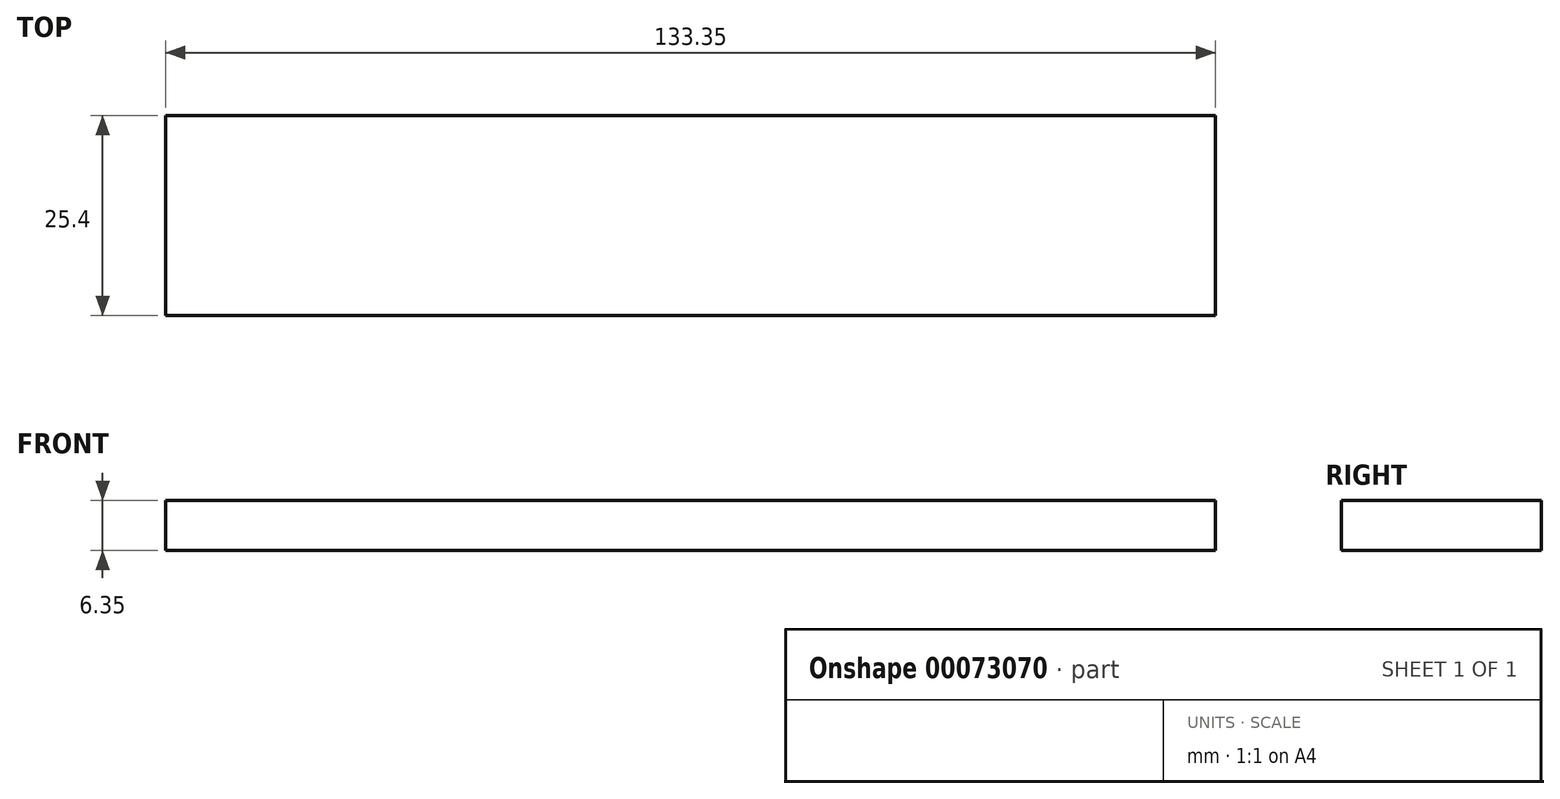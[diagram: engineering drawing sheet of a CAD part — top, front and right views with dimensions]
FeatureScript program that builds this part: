
annotation { "Feature Type Name" : "Feature", "Feature Type Description" : "" }
export const myFeature = defineFeature(function(context is Context, id is Id, definition is map)
    precondition{}
    {
        {
            var Q0;
            Q0=qCreatedBy(makeId("Top.planeOp"),FACE);
            var sketch = newSketch(context, id + "F0", { "sketchPlane" : qUnion([Q0])});
            skLineSegment(sketch, "E0.bottom", {"start": v(0, 0) * mm, "end": v(-133.35, 0) * mm});
            skLineSegment(sketch, "E0.top", {"start": v(0, 25.4) * mm, "end": v(-133.35, 25.4) * mm});
            skLineSegment(sketch, "E0.left", {"start": v(0, 0) * mm, "end": v(0, 25.4) * mm});
            skLineSegment(sketch, "E0.right", {"start": v(-133.35, 0) * mm, "end": v(-133.35, 25.4) * mm});
            skSolve(sketch);
        }
        {
            var Q0;
            Q0 = qSketchRegion(id + "F0", true);
            extrude(context, id + "F1", {"entities" : qUnion([Q0]), "depth" : 6.35 * mm});
        }
    });
